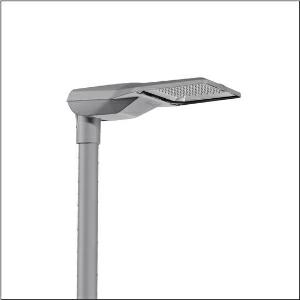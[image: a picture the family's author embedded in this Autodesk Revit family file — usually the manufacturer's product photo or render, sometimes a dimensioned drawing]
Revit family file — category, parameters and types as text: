
# Revit family: streetlight_sl_21_midi___stw1_0a_5xe7e33a08nb_8300
name_source: partatom
category: Lighting Fixtures
units: mm (PartAtom-declared; Revit-internal decimal feet)

## family parameters
Cut with Voids When Loaded = No
Host = Face
Light Source = No
Part Type = Normal
Room Calculation Point = No
Round Connector Dimension = Use Diameter
Shared = No

## types (1)
- --- (1 x LED, 22700 lm, 151.2 W, 3000K)
    Apparent Load = 151 VA
    CIE Flux Codes = 39 75 98 100 100
    Color Rendering = 70
    Color Temperature = 3000K
    Default Elevation = 1800 mm
    Description = Streetlight SL 21 midi, mast luminaire, primary light control with lens, of PMMA, primary optical cover: cover, of toughened safety glass, transparent, light distribution: STW1.0a, light emission: direct distribution, primary light characteristic: asymmetric, installation type: post-top, side-entry, LED, 3G 1.5mm², High Power LED, rated luminous flux: 22.700lm, luminous efficacy: 150lm/W, light colour: 730, colour temperature: 3000K, control: overheat protection, constant luminous flux control, time-dependent luminous flux control, flexible luminous flux parameterisation, mains connection: 220..240V, AC, 50/60Hz, connection cable pre-assembled, cable length: 12,5m, wiring characteristics: H07RN-F, start of lifetime: 151W, end of service life: 157W, reduction: 70W, luminaire housing, of diecast aluminium, powder-coated, Siteco® metallic grey (DB 702S), corrosivity category C5 mid according to DIN EN ISO 12944, please order mast flange separately, inclination adjustable: 0°, 5°, 10°, 15°, sealing non-destructively replaceable, multi-level sealing system, length: 644mm, width: 335mm, height: 110mm, mast flange for spigot size: 42mm (side-entry): 5XC10008XM4, 60/48mm (side-entry/post-top): 5XC10108XM2, 76/60mm (side-entry/post-top): 5XC10108XM1, protection rating (complete): IP66, insulation class (complete): insulation class II (safety insulation), certification: CE, ENEC, ENEC+, VDE, impact resistance: IK09, permissible operating ambient temperature for outdoor applications: -40..+50°C, standard-compliant lighting for roads and squares, packaging unit: 1 piece

Light Distribution: STW1.0a
    Height = 111 mm
    Lamp = 1 x LED
    Lamp Light Flux = 22700 lm
    Lamp Power = 151.2 W
    Lamp count = 1
    Length = 644 mm
    Luminous efficacy = 150 lm/W
    Manufacturer = Siteco
    ModVariant = No
    Model = 5XE7E33A08NB
    Number of Poles = 1
    OnlyDefault = Yes
    Power Factor = 1
    Product Name = Streetlight SL 21 midi | STW1.0a
    Product group = mast luminaire | pylon top
    ProductGroupID = 6100
    Protection Class = Protection class II
    Protection Degree = IP 66
    RLX_Detail_Level = 1
    RLX_Emergency_Light_Flux = 0 lm
    RLX_Emergency_Type = 0
    RLX_Emergency_Type_DB = No
    RlxData = <blob elided: 91085 chars, md5=4d533a7d>
    Socket = socket
    Standby Power = 0 W
    System Light Flux = 22700 lm
    System Power = 151 W
    Type Comments = factory setting: luminous flux: 100 % | Output Level: 100 % | 802 mA
    Type Image = l_1004298.jpg
    URL = http://relux.com
    VarID = @adj_102001
    Voltage = 0 V
    Weight = 0.00 kg
    Width = 336 mm

## geometry (parser evidence)
native form markers: Blend x4, Sweep x10
no freeform markers — native parametric forms only
